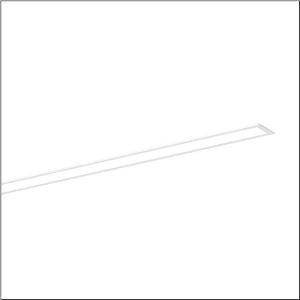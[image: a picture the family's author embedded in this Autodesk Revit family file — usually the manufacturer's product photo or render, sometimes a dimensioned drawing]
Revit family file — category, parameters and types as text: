
# Revit family: silica_r__21_51mx10dc45wb_eef5
name_source: partatom
category: Lighting Fixtures
units: mm (PartAtom-declared; Revit-internal decimal feet)

## family parameters
Cut with Voids When Loaded = No
Host = Face
Light Source = No
Part Type = Normal
Room Calculation Point = No
Round Connector Dimension = Use Diameter
Shared = No

## types (1)
- --- (1 x LED, 6000 lm, 40.1 W, 4000K)
    Apparent Load = 40 VA
    CIE Flux Codes = 48 79 96 100 100
    Color Rendering = 80
    Color Temperature = 4000K
    Default Elevation = 1800 mm
    Description = Silica® 21, office luminaire, primary optical cover: cover, of PMMA, opal, light emission: direct distribution, primary light characteristic: symmetric, installation type: recessed, LED, rated luminous flux: 6.000lm, luminous efficacy: 150lm/W, light colour: 840, colour temperature: 4000K, with terminal, 3+2-pole, max. 2.5mm², mains connection: 220..240V, AC, 50/60Hz, rated input power: 40.1W, luminaire housing, of aluminium, traffic white (RAL 9016), length: 3.028mm, width: 79mm, height: 53mm, protection rating (complete): IP20, insulation class (complete): insulation class I (protective earthing), certification: CE, permissible operating ambient temperature: 0..+35°C, standard: EN 50419, packaging unit: 1 piece
    Height = 0 mm  [stored 0 ft]
    Lamp = 1 x LED
    Lamp Light Flux = 6000 lm
    Lamp Power = 40.1 W
    Lamp count = 1
    Length = 3027 mm
    Luminous efficacy = 150 lm/W
    Manufacturer = Siteco
    ModVariant = No
    Model = 51MX10DC45WB
    Mounting Place = Ceiling
    Mounting Type = Recessed
    Number of Poles = 1
    OnlyDefault = Yes
    Power Factor = 1
    Product Name = Silica® 21
    Product group = office luminaire | ceiling recessed
    ProductGroupID = 401
    Protection Class = Protection class I
    Protection Degree = IP 20
    RLX_Detail_Level = 1
    RLX_Emergency_Light_Flux = 0 lm
    RLX_Emergency_Type = 0
    RLX_Emergency_Type_DB = No
    RlxData = <blob elided: 21217 chars, md5=ccb54b07>
    Socket = socket
    Standby Power = 0 W
    System Light Flux = 6000 lm
    System Power = 40 W
    Type Comments = factory setting: luminous flux: 100 % | dim-lin: 254 | 218 mA
    Type Image = l_1297737.jpg
    URL = http://relux.com
    VarID = @adj_047593
    Voltage = 0 V
    Weight = 0.00 kg
    Width = 79 mm

note: [stored X ft] marks values corroborated as IEEE doubles in the binary element streams (Revit-internal decimal feet)

## geometry (parser evidence)
native form markers: Blend x4, Sweep x10
no freeform markers — native parametric forms only
